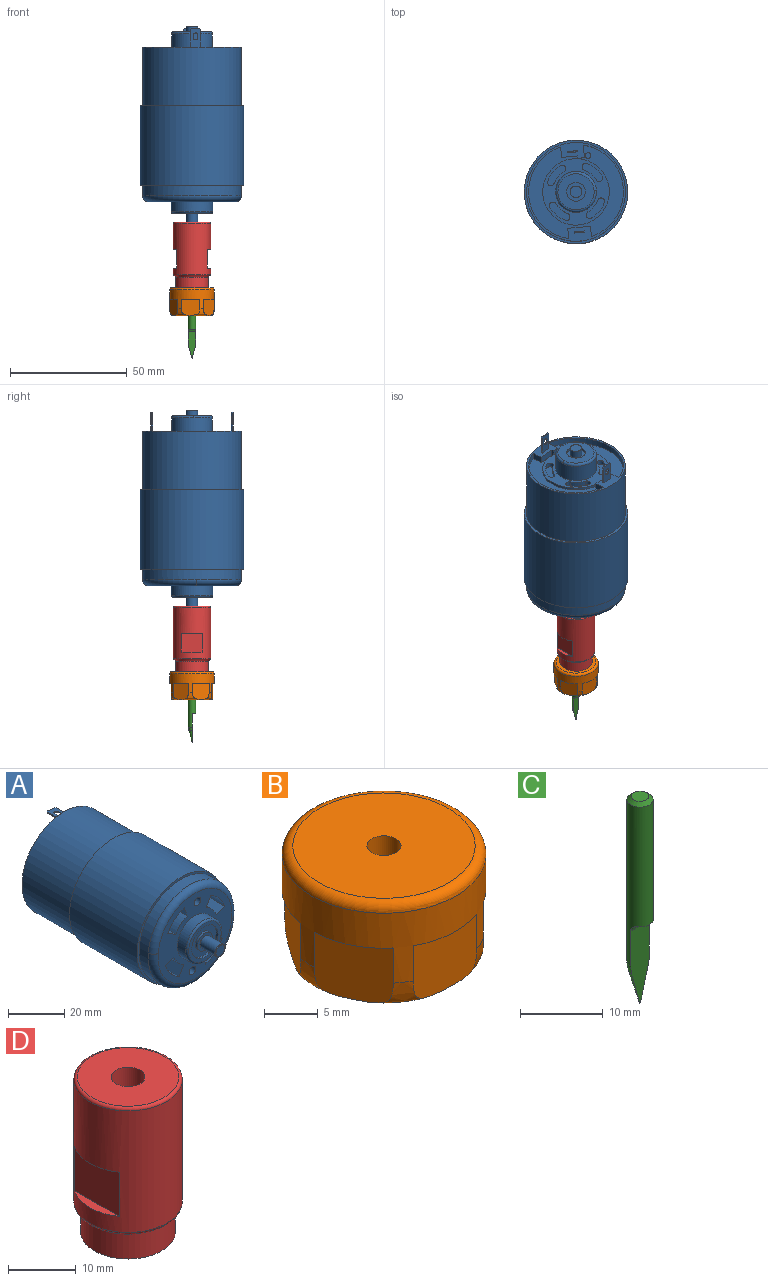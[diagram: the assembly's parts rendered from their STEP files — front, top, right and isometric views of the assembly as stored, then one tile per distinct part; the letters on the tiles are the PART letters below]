
ASSEMBLY  parts=4 mates=3
PART A: 110 faces, bbox 45.6x88x45.6 mm
  f0: torus R=18.65mm, axis (0,1,0), area 249.7mm2, adj f6,f28,f41
  f1: torus R=8.15mm, axis (0,1,0), area 31.9mm2, adj f8,f79,f85
  f2: torus R=7.75mm, axis (0,-1,0), area 41.4mm2, adj f19,f102,f104
  f3: torus R=2.25mm, axis (0,1,0), area 3mm2, adj f23,f107,f109
  f4: cylinder r=22.15mm len=44.3mm, axis (0,1,0), area 4731.9mm2, adj f25,f26
  f5: cylinder r=21.15mm len=42.3mm, axis (0,-1,0), area 3322.2mm2, adj f25,f27
  f6: cylinder r=21.15mm len=42.3mm, axis (0,-1,0), area 611.3mm2, adj f0,f26,f28
  f7: cylinder r=20.3mm len=39.26mm, axis (0,1,0), area 151mm2, adj f27,f31,f38,f51
  f8: cylinder r=8.9mm len=17.8mm, axis (0,-1,0), area 237.7mm2, adj f1,f41,f79
  f9: cylinder r=1.65mm len=11.5mm, axis (0,-1,0), area 119.2mm2, adj f13,f41
  f10: cylinder r=1.65mm len=11.5mm, axis (0,-1,0), area 119.2mm2, adj f14,f41
  f11: cylinder r=14.25mm len=28.5mm, axis (0,1,0), area 89.5mm2, adj f51,f83
  f12: cylinder r=1.25mm len=2.5mm, axis (0,1,0), area 0.8mm2, adj f51,f84
  f13: cone r=1.65mm half-angle=59deg, axis (0,-1,0), area 10mm2, adj f9
  f14: cone r=1.65mm half-angle=59deg, axis (0,-1,0), area 10mm2, adj f10
  f15: cylinder r=1.5mm len=2.9mm, axis (0,1,0), area 9.4mm2, adj f83,f86,f87,f98
  f16: cylinder r=1.5mm len=2.9mm, axis (0,1,0), area 9.4mm2, adj f83,f89,f90,f99
  f17: cylinder r=1.5mm len=2.79mm, axis (0,1,0), area 9.4mm2, adj f83,f92,f94,f100
  f18: cylinder r=1.5mm len=2.79mm, axis (0,1,0), area 9.4mm2, adj f83,f95,f97,f101
  f19: cylinder r=8.75mm len=17.5mm, axis (0,-1,0), area 412.3mm2, adj f2,f83,f102
  f20: cylinder r=6.62mm len=13.25mm, axis (0,-1,0), area 41.6mm2, adj f85,f103
  f21: cylinder r=3.75mm len=7.5mm, axis (0,-1,0), area 23.6mm2, adj f103,f105
  f22: cylinder r=4mm len=8mm, axis (0,1,0), area 25.1mm2, adj f104,f106
  f23: cylinder r=2.5mm len=7.55mm, axis (0,-1,0), area 118.6mm2, adj f3,f105,f107
  f24: cylinder r=2.5mm len=5mm, axis (0,-1,0), area 53.4mm2, adj f106,f108
  f25: plane 44.3x44.3mm, normal (0,1,0), area 136mm2, adj f4,f5
  f26: plane 44.3x44.3mm, normal (0,-1,0), area 136mm2, adj f4,f6
  f27: plane 42.3x42.3mm, normal (0,1,0), area 203.5mm2, adj f5,f7,f29,f30,f31,f32,f33,f34
  f28: torus R=18.65mm, axis (0,1,0), area 249.7mm2, adj f0,f6,f41
  f29: plane 8.15x4.58mm, normal (0.09,0,1), area 32.1mm2, adj f27,f42,f43,f44,f45,f46,f47,f48
  f30: plane 8.15x4.58mm, normal (-0.09,0,-1), area 32.1mm2, adj f27,f42,f43,f44,f45,f46,f47,f48
  f31: plane 4.44x2.8mm, normal (1,0,-0.09), area 12.5mm2, adj f7,f27,f32,f51
  f32: plane 9.71x2.8mm, normal (-0.09,0,-1), area 27.3mm2, adj f27,f31,f33,f51
  f33: plane 4.44x2.8mm, normal (-1,0,0.09), area 12.5mm2, adj f27,f32,f34,f51
  f34: cylinder r=20.3mm len=39.26mm, axis (0,1,0), area 151mm2, adj f27,f33,f35,f51
  f35: plane 4.44x2.8mm, normal (-1,0,0.09), area 12.5mm2, adj f27,f34,f36,f51
  f36: plane 6.92x2.8mm, normal (0.09,0,1), area 19.4mm2, adj f27,f35,f51,f52
  f37: plane 2.8x2.8mm, normal (0.09,0,1), area 7.9mm2, adj f27,f38,f51,f52
  f38: plane 5.44x2.8mm, normal (1,0,-0.09), area 15.3mm2, adj f7,f27,f37,f51
  f39: plane 8.15x4.58mm, normal (-0.09,0,-1), area 32.1mm2, adj f27,f53,f54,f55,f56,f57,f58,f59
  f40: plane 8.15x4.58mm, normal (0.09,0,1), area 32.1mm2, adj f27,f53,f54,f55,f56,f57,f58,f59
  f41: plane 37.3x37.3mm, normal (0,-1,0), area 647.6mm2, adj f0,f8,f9,f10,f28,f62,f63,f64
  f42: plane 3.63x0.81mm, normal (0,1,0), area 1.8mm2, adj f29,f30,f43,f46
  f43: plane 0.54x0.54mm, normal (-0.7,0.71,0.06), area 0.4mm2, adj f29,f30,f42,f44
  f44: plane 7.65x0.5mm, normal (-1,0,0.09), area 3.8mm2, adj f27,f29,f30,f43
  f45: plane 7.65x0.5mm, normal (1,0,-0.09), area 3.8mm2, adj f27,f29,f30,f46
  f46: plane 0.54x0.54mm, normal (0.7,0.71,-0.06), area 0.4mm2, adj f29,f30,f42,f45
  f47: plane 1x0.5mm, normal (1,0,-0.09), area 0.5mm2, adj f29,f30,f48,f50
  f48: cylinder r=1mm len=2.04mm, axis (0.09,0,1), area 1.6mm2, adj f29,f30,f47,f49
  f49: plane 1x0.5mm, normal (-1,0,0.09), area 0.5mm2, adj f29,f30,f48,f50
  f50: cylinder r=1mm len=2.04mm, axis (0.09,0,1), area 1.6mm2, adj f29,f30,f47,f49
  f51: plane 40.6x40.11mm, normal (0,1,0), area 554.3mm2, adj f7,f11,f12,f31,f32,f33,f34,f35
  f52: plane 2.8x1mm, normal (-1,0,0.09), area 2.8mm2, adj f27,f36,f37,f51
  f53: plane 7.65x0.5mm, normal (-1,0,0.09), area 3.8mm2, adj f27,f39,f40,f54
  f54: plane 0.54x0.54mm, normal (-0.7,0.71,0.06), area 0.4mm2, adj f39,f40,f53,f55
  f55: plane 3.63x0.81mm, normal (0,1,0), area 1.8mm2, adj f39,f40,f54,f56
  f56: plane 0.54x0.54mm, normal (0.7,0.71,-0.06), area 0.4mm2, adj f39,f40,f55,f57
  f57: plane 7.65x0.5mm, normal (1,0,-0.09), area 3.8mm2, adj f27,f39,f40,f56
  f58: plane 1x0.5mm, normal (-1,0,0.09), area 0.5mm2, adj f39,f40,f59,f61
  f59: cylinder r=1mm len=2.04mm, axis (-0.09,0,-1), area 1.6mm2, adj f39,f40,f58,f60
  f60: plane 1x0.5mm, normal (1,0,-0.09), area 0.5mm2, adj f39,f40,f59,f61
  f61: cylinder r=1mm len=2.04mm, axis (-0.09,0,-1), area 1.6mm2, adj f39,f40,f58,f60
  f62: plane 10x4.42mm, normal (-0.94,0,-0.34), area 47mm2, adj f41,f63,f65,f78
  f63: cylinder r=11.3mm len=10mm, axis (0,-1,0), area 78.9mm2, adj f41,f62,f64,f78
  f64: plane 10x4.07mm, normal (0.5,0,0.87), area 47mm2, adj f41,f63,f65,f78
  f65: cylinder r=16mm len=10mm, axis (0,-1,0), area 111.7mm2, adj f41,f62,f64,f78
  f66: cylinder r=16mm len=10mm, axis (0,-1,0), area 111.7mm2, adj f41,f67,f69,f80
  f67: plane 10x4.42mm, normal (0.94,0,0.34), area 47mm2, adj f41,f66,f68,f80
  f68: cylinder r=11.3mm len=10mm, axis (0,-1,0), area 78.9mm2, adj f41,f67,f69,f80
  f69: plane 10x4.07mm, normal (-0.5,0,-0.87), area 47mm2, adj f41,f66,f68,f80
  f70: plane 10x4.42mm, normal (-0.34,0,0.94), area 47mm2, adj f41,f71,f73,f81
  f71: cylinder r=11.3mm len=10mm, axis (0,-1,0), area 78.9mm2, adj f41,f70,f72,f81
  f72: plane 10x4.07mm, normal (0.87,0,-0.5), area 47mm2, adj f41,f71,f73,f81
  f73: cylinder r=16mm len=10mm, axis (0,-1,0), area 111.7mm2, adj f41,f70,f72,f81
  f74: cylinder r=16mm len=10mm, axis (0,-1,0), area 111.7mm2, adj f41,f75,f77,f82
  f75: plane 10x4.42mm, normal (0.34,0,-0.94), area 47mm2, adj f41,f74,f76,f82
  f76: cylinder r=11.3mm len=10mm, axis (0,-1,0), area 78.9mm2, adj f41,f75,f77,f82
  f77: plane 10x4.07mm, normal (-0.87,0,0.5), area 47mm2, adj f41,f74,f76,f82
  f78: plane 9.99x9.39mm, normal (0,-1,0), area 44.8mm2, adj f62,f63,f64,f65
  f79: torus R=8.15mm, axis (0,1,0), area 31.9mm2, adj f1,f8,f85
  f80: plane 9.99x9.39mm, normal (0,-1,0), area 44.8mm2, adj f66,f67,f68,f69
  f81: plane 9.99x9.39mm, normal (0,-1,0), area 44.8mm2, adj f70,f71,f72,f73
  f82: plane 9.99x9.39mm, normal (0,-1,0), area 44.8mm2, adj f74,f75,f76,f77
  f83: plane 28.5x28.5mm, normal (0,1,0), area 276.5mm2, adj f11,f15,f16,f17,f18,f19,f86,f87
  f84: plane 2.5x2.5mm, normal (0,1,0), area 4.9mm2, adj f12
  f85: plane 16.3x16.3mm, normal (0,-1,0), area 70.8mm2, adj f1,f20,f79
  f86: cylinder r=13mm len=6.56mm, axis (0,1,0), area 17.5mm2, adj f15,f83,f88,f98
  f87: cylinder r=10mm len=5.05mm, axis (0,1,0), area 13.4mm2, adj f15,f83,f88,f98
  f88: cylinder r=1.5mm len=2.79mm, axis (0,1,0), area 9.4mm2, adj f83,f86,f87,f98
  f89: cylinder r=13mm len=6.56mm, axis (0,1,0), area 17.5mm2, adj f16,f83,f91,f99
  f90: cylinder r=10mm len=5.05mm, axis (0,1,0), area 13.4mm2, adj f16,f83,f91,f99
  f91: cylinder r=1.5mm len=2.79mm, axis (0,1,0), area 9.4mm2, adj f83,f89,f90,f99
  f92: cylinder r=13mm len=6.56mm, axis (0,1,0), area 17.5mm2, adj f17,f83,f93,f100
  f93: cylinder r=1.5mm len=2.9mm, axis (0,1,0), area 9.4mm2, adj f83,f92,f94,f100
  f94: cylinder r=10mm len=5.05mm, axis (0,1,0), area 13.4mm2, adj f17,f83,f93,f100
  f95: cylinder r=13mm len=6.56mm, axis (0,1,0), area 17.5mm2, adj f18,f83,f96,f101
  f96: cylinder r=1.5mm len=2.9mm, axis (0,1,0), area 9.4mm2, adj f83,f95,f97,f101
  f97: cylinder r=10mm len=5.05mm, axis (0,1,0), area 13.4mm2, adj f18,f83,f96,f101
  f98: plane 8.8x7.87mm, normal (0,1,0), area 30.2mm2, adj f15,f86,f87,f88
  f99: plane 8.8x7.87mm, normal (0,1,0), area 30.2mm2, adj f16,f89,f90,f91
  f100: plane 8.8x7.87mm, normal (0,1,0), area 30.2mm2, adj f17,f92,f93,f94
  f101: plane 8.8x7.87mm, normal (0,1,0), area 30.2mm2, adj f18,f95,f96,f97
  f102: torus R=7.75mm, axis (0,-1,0), area 41.4mm2, adj f2,f19,f104
  f103: plane 13.25x13.25mm, normal (0,-1,0), area 93.7mm2, adj f20,f21
  f104: plane 15.5x15.5mm, normal (0,1,0), area 138.4mm2, adj f2,f22,f102
  f105: plane 7.5x7.5mm, normal (0,-1,0), area 24.5mm2, adj f21,f23
  f106: plane 8x8mm, normal (0,1,0), area 30.6mm2, adj f22,f24
  f107: torus R=2.25mm, axis (0,1,0), area 3mm2, adj f3,f23,f109
  f108: plane 5x5mm, normal (0,1,0), area 19.6mm2, adj f24
  f109: plane 4.5x4.5mm, normal (0,-1,0), area 15.9mm2, adj f3,f107
PART B: 19 faces, bbox 20.6x20.6x12 mm
  f0: cylinder r=9.5mm len=19mm, axis (0,0,1), area 284.4mm2, adj f3,f4,f5,f6,f7,f8,f9,f10
  f1: plane 17x17mm, normal (0,0,1), area 219.1mm2, adj f2,f15
  f2: cylinder r=1.59mm len=11.5mm, axis (0,0,-1), area 114.7mm2, adj f1,f18
  f3: plane 7.02x3.42mm, normal (0,0,-1), area 4.4mm2, adj f0,f4
  f4: plane 7.02x6.8mm, normal (-0.9,-0.44,0), area 50.7mm2, adj f0,f3,f16
  f5: plane 7.79x1.14mm, normal (0,0,-1), area 4.4mm2, adj f0,f6
  f6: plane 7.79x6.79mm, normal (-0.07,-1,0), area 50.8mm2, adj f0,f5,f16
  f7: plane 6.47x4.37mm, normal (0,0,-1), area 4.4mm2, adj f0,f8
  f8: plane 6.79x6.48mm, normal (0.83,-0.56,0), area 50.7mm2, adj f0,f7,f16
  f9: plane 7.02x3.42mm, normal (0,0,-1), area 4.4mm2, adj f0,f10
  f10: plane 7.02x6.8mm, normal (0.9,0.44,0), area 50.7mm2, adj f0,f9,f16
  f11: plane 7.79x1.14mm, normal (0,0,-1), area 4.4mm2, adj f0,f12
  f12: plane 7.79x6.79mm, normal (0.07,1,0), area 50.8mm2, adj f0,f11,f16
  f13: plane 6.47x4.37mm, normal (0,0,-1), area 4.4mm2, adj f0,f14
  f14: plane 6.79x6.48mm, normal (-0.83,0.56,0), area 50.7mm2, adj f0,f13,f16
  f15: torus R=8.5mm, axis (0,0,-1), area 90.2mm2, adj f0,f1
  f16: bspline ~18.97x18.97mm, area 156.6mm2, adj f0,f4,f6,f8,f10,f12,f14,f17
  f17: extruded ~12.93x12.93mm, area 20.4mm2, adj f16,f18
  f18: plane 13.1x13.1mm, normal (0,0,-1), area 124.7mm2, adj f2,f17
PART C: 9 faces, bbox 3.2x3.2x30.6 mm
  f0: cylinder r=1.59mm len=23.84mm, axis (0,0,-1), area 207.9mm2, adj f3,f5,f6,f7,f8
  f1: cone r=1.59mm half-angle=15deg, axis (0,0,1), area 12.1mm2, adj f2,f3,f7
  f2: sphere r=0.1mm, area 0mm2, adj f1,f7
  f3: revolved ~3.18x1.59mm, area 6.3mm2, adj f0,f1,f7
  f4: plane 2.18x2.18mm, normal (0,0,1), area 3.7mm2, adj f8
  f5: cylinder r=1mm len=3.18mm, axis (1,0,0), area 4.7mm2, adj f0,f6,f7
  f6: plane 2.47x0.59mm, normal (0,0,-1), area 1mm2, adj f0,f5
  f7: plane 11.38x3.18mm, normal (0,-1,0), area 27.6mm2, adj f0,f1,f2,f3,f5
  f8: cone r=1.09mm half-angle=45deg, axis (0,0,-1), area 5.9mm2, adj f0,f4
PART D: 16 faces, bbox 17.3x17.3x28 mm
  f0: cylinder r=1.59mm len=3.18mm, axis (0,0,-1), area 29.9mm2, adj f4,f5
  f1: cylinder r=8mm len=22mm, axis (0,0,-1), area 946.5mm2, adj f8,f9,f10,f11,f12,f13,f14,f15
  f2: plane 15x15mm, normal (0,0,1), area 157.1mm2, adj f6,f9
  f3: cylinder r=7mm len=14mm, axis (0,0,-1), area 197.9mm2, adj f4,f7
  f4: plane 14x14mm, normal (0,0,-1), area 146mm2, adj f0,f3
  f5: plane 5x5mm, normal (0,0,1), area 11.7mm2, adj f0,f6
  f6: cylinder r=2.5mm len=25mm, axis (0,0,1), area 392.7mm2, adj f2,f5
  f7: torus R=7.5mm, axis (0,0,1), area 35.4mm2, adj f3,f8
  f8: torus R=7.5mm, axis (0,0,1), area 38.6mm2, adj f1,f7
  f9: torus R=7.5mm, axis (0,0,1), area 38.6mm2, adj f1,f2
  f10: plane 9.33x1.5mm, normal (0,0,-1), area 9.5mm2, adj f1,f12
  f11: plane 9.33x1.5mm, normal (0,0,1), area 9.5mm2, adj f1,f12
  f12: plane 9.33x8mm, normal (-1,0,0), area 74.6mm2, adj f1,f10,f11
  f13: plane 9.33x1.5mm, normal (0,0,-1), area 9.5mm2, adj f1,f14
  f14: plane 9.33x8mm, normal (1,0,0), area 74.6mm2, adj f1,f13,f15
  f15: plane 9.33x1.5mm, normal (0,0,1), area 9.5mm2, adj f1,f14
PLACE A rot(axis=(1,0,0),90deg) t=(3.5,-61.08,49.98)mm
PLACE B t=(0,0,-23.97)mm
PLACE C t=(0,0,-48.47)mm
PLACE D t=(0,0,-23.97)mm
MATE fastened A.f102 <-> D.f0  axis (0,0,-1) through (0,0,4.03)mm
MATE fastened B.f0 <-> D.f0  axis (0,0,1) through (0,0,-23.97)mm
MATE fastened B.f0 <-> C.f1  axis (0,0,-1) through (0,0,-23.97)mm
